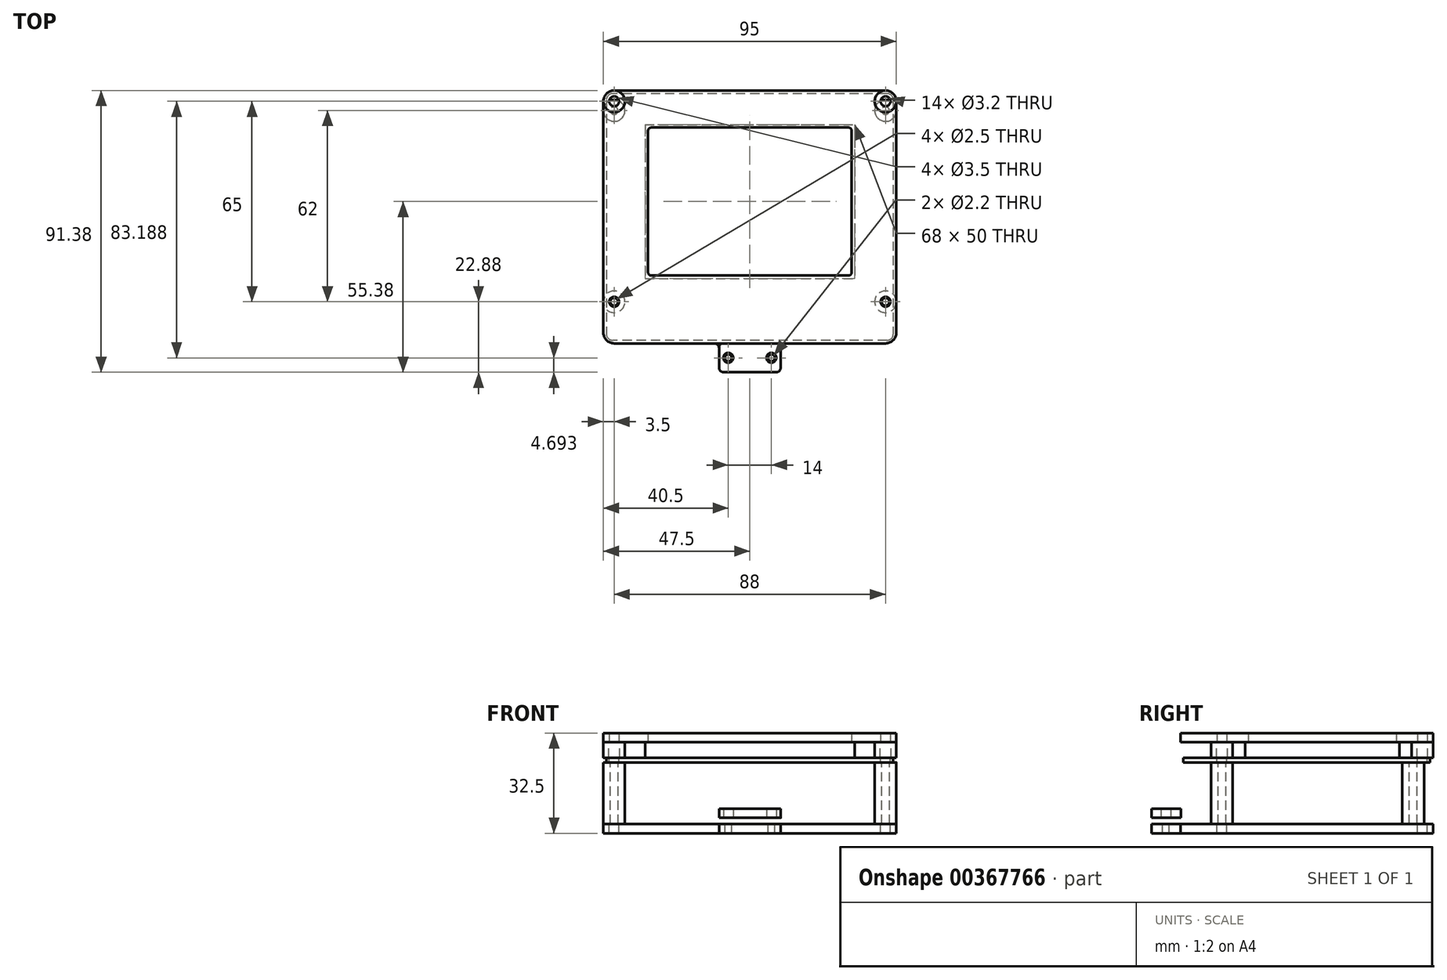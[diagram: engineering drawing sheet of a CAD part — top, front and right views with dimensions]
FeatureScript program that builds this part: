
annotation { "Feature Type Name" : "Feature", "Feature Type Description" : "" }
export const myFeature = defineFeature(function(context is Context, id is Id, definition is map)
    precondition{}
    {
        {
            var Q0;
            Q0=qCreatedBy(makeId("Top.planeOp"),FACE);
            var sketch = newSketch(context, id + "F0", { "sketchPlane" : qUnion([Q0])});
            skLineSegment(sketch, "E0.bottom", {"start": v(44, -41) * mm, "end": v(-44, -41) * mm});
            skLineSegment(sketch, "E0.top", {"start": v(44, 41) * mm, "end": v(-44, 41) * mm});
            skLineSegment(sketch, "E0.left", {"start": v(47.5, -37.5) * mm, "end": v(47.5, 37.5) * mm});
            skLineSegment(sketch, "E0.right", {"start": v(-47.5, -37.5) * mm, "end": v(-47.5, 37.5) * mm});
            skPoint(sketch, "E0.middle", {"position": v(0, 0) * mm});
            skLineSegment(sketch, "E1.top", {"start": v(44, 37.5) * mm, "end": v(-44, 37.5) * mm, "construction": true});
            skLineSegment(sketch, "E1.left", {"start": v(44, -27.5) * mm, "end": v(44, 37.5) * mm, "construction": true});
            skLineSegment(sketch, "E1.right", {"start": v(-44, -27.5) * mm, "end": v(-44, 37.5) * mm, "construction": true});
            skLineSegment(sketch, "E2", {"start": v(-44, -27.5) * mm, "end": v(44, -27.5) * mm, "construction": true});
            skPoint(sketch, "E1.bottom.end.orphan", {"position": v(-44, -37.5) * mm});
            skPoint(sketch, "E3.orphan", {"position": v(44, -37.5) * mm});
            skCircle(sketch, "E4", {"center": v(-44, 37.5) * mm, "radius": 1.6 * mm});
            skCircle(sketch, "E5", {"center": v(44, 37.5) * mm, "radius": 1.6 * mm});
            skCircle(sketch, "E6", {"center": v(44, -27.5) * mm, "radius": 1.6 * mm});
            skCircle(sketch, "E7", {"center": v(-44, -27.5) * mm, "radius": 1.6 * mm});
            skArc(sketch, "E8", {"start": v(-44, 41) * mm, "mid": v(-46.47, 39.97) * mm, "end": v(-47.5, 37.5) * mm});
            skArc(sketch, "E9", {"start": v(47.5, 37.5) * mm, "mid": v(46.47, 39.97) * mm, "end": v(44, 41) * mm});
            skPoint(sketch, "E10.visualSharp", {"position": v(47.5, -41) * mm});
            skArc(sketch, "E10.filletArc", {"start": v(44, -41) * mm, "mid": v(46.47, -39.97) * mm, "end": v(47.5, -37.5) * mm});
            skPoint(sketch, "E11.visualSharp", {"position": v(-47.5, -41) * mm});
            skArc(sketch, "E11.filletArc", {"start": v(-47.5, -37.5) * mm, "mid": v(-46.47, -39.97) * mm, "end": v(-44, -41) * mm});
            skPoint(sketch, "E12.orphan", {"position": v(-47.5, 41) * mm});
            skPoint(sketch, "E13.orphan", {"position": v(47.5, 41) * mm});
            skLineSegment(sketch, "E14.bottom", {"start": v(-32, 29) * mm, "end": v(32, 29) * mm});
            skLineSegment(sketch, "E14.top", {"start": v(-32, -19) * mm, "end": v(32, -19) * mm});
            skLineSegment(sketch, "E14.left", {"start": v(-33, 28) * mm, "end": v(-33, -18) * mm});
            skLineSegment(sketch, "E14.right", {"start": v(33, 28) * mm, "end": v(33, -18) * mm});
            skPoint(sketch, "E15.visualSharp", {"position": v(-33, 29) * mm});
            skArc(sketch, "E15.filletArc", {"start": v(-32, 29) * mm, "mid": v(-32.7, 28.7) * mm, "end": v(-33, 28) * mm});
            skPoint(sketch, "E16.visualSharp", {"position": v(33, 29) * mm});
            skArc(sketch, "E16.filletArc", {"start": v(33, 28) * mm, "mid": v(32.7, 28.7) * mm, "end": v(32, 29) * mm});
            skPoint(sketch, "E17.visualSharp", {"position": v(33, -19) * mm});
            skArc(sketch, "E17.filletArc", {"start": v(32, -19) * mm, "mid": v(32.7, -18.7) * mm, "end": v(33, -18) * mm});
            skPoint(sketch, "E18.visualSharp", {"position": v(-33, -19) * mm});
            skArc(sketch, "E18.filletArc", {"start": v(-33, -18) * mm, "mid": v(-32.7, -18.7) * mm, "end": v(-32, -19) * mm});
            skSolve(sketch);
        }
        {
            var Q0;
            Q0=makeQuery(id+"F0.imprint","IMPRINT",FACE,{"disambiguationData":[TD([[makeQuery(id+"F0.imprint","IMPRINT",EDGE,{"derivedFrom":sQuery(id+"F0.wireOp",EDGE,"E0.bottom")}),-1.0]])]});
            extrude(context, id + "F1", {"entities" : qUnion([Q0]), "depth" : 3 * mm});
        }
        {
            var Q0;
            Q0=makeQuery(id+"F1.opExtrude","CAP_FACE",FACE,{"disambiguationData":[OSD([sQuery(id+"F0.wireOp",EDGE,"E0.bottom"),sQuery(id+"F0.wireOp",EDGE,"E0.top"),sQuery(id+"F0.wireOp",EDGE,"E0.left"),sQuery(id+"F0.wireOp",EDGE,"E0.right"),sQuery(id+"F0.wireOp",EDGE,"E4"),sQuery(id+"F0.wireOp",EDGE,"E5"),sQuery(id+"F0.wireOp",EDGE,"E6"),sQuery(id+"F0.wireOp",EDGE,"E7"),sQuery(id+"F0.wireOp",EDGE,"E8"),sQuery(id+"F0.wireOp",EDGE,"E9"),sQuery(id+"F0.wireOp",EDGE,"E10.filletArc"),sQuery(id+"F0.wireOp",EDGE,"E11.filletArc"),sQuery(id+"F0.wireOp",EDGE,"E14.bottom"),sQuery(id+"F0.wireOp",EDGE,"E14.top"),sQuery(id+"F0.wireOp",EDGE,"E14.left"),sQuery(id+"F0.wireOp",EDGE,"E14.right"),sQuery(id+"F0.wireOp",EDGE,"E15.filletArc"),sQuery(id+"F0.wireOp",EDGE,"E16.filletArc"),sQuery(id+"F0.wireOp",EDGE,"E17.filletArc"),sQuery(id+"F0.wireOp",EDGE,"E18.filletArc")])],"isStart":true});
            var sketch = newSketch(context, id + "F2", { "sketchPlane" : qUnion([Q0])});
            skCircle(sketch, "E19", {"center": v(-44, 27.5) * mm, "radius": 1.75 * mm});
            skCircle(sketch, "E20", {"center": v(44, 27.5) * mm, "radius": 1.75 * mm});
            skCircle(sketch, "E21", {"center": v(44, -37.5) * mm, "radius": 1.75 * mm});
            skCircle(sketch, "E22", {"center": v(-44, -37.5) * mm, "radius": 1.75 * mm});
            skCircle(sketch, "E23", {"center": v(-44, -37.5) * mm, "radius": 3.5 * mm});
            skCircle(sketch, "E24", {"center": v(44, -37.5) * mm, "radius": 3.5 * mm});
            skCircle(sketch, "E25", {"center": v(44, 27.5) * mm, "radius": 3.5 * mm});
            skCircle(sketch, "E26", {"center": v(-44, 27.5) * mm, "radius": 3.5 * mm});
            skSolve(sketch);
        }
        {
            var Q0;
            Q0=qSketchRegion(id+"F2",true);
            extrude(context, id + "F3", {"entities" : qUnion([Q0]), "depth" : 5 * mm});
        }
        {
            var Q0;
            Q0=makeQuery(id+"F3.opExtrude","CAP_FACE",FACE,{"disambiguationData":[OSD([sQuery(id+"F2.wireOp",EDGE,"E19"),sQuery(id+"F2.wireOp",EDGE,"E26")])],"isStart":false});
            var sketch = newSketch(context, id + "F4", { "sketchPlane" : qUnion([Q0])});
            skLineSegment(sketch, "E27.bottom", {"start": v(44.5, -40) * mm, "end": v(-44.5, -40) * mm});
            skLineSegment(sketch, "E27.top", {"start": v(44.5, 40) * mm, "end": v(-44.5, 40) * mm});
            skLineSegment(sketch, "E27.left", {"start": v(46.5, -38) * mm, "end": v(46.5, 38) * mm});
            skLineSegment(sketch, "E27.right", {"start": v(-46.5, -38) * mm, "end": v(-46.5, 38) * mm});
            skPoint(sketch, "E27.middle", {"position": v(0, 0) * mm});
            skPoint(sketch, "E28.visualSharp", {"position": v(-46.5, 40) * mm});
            skArc(sketch, "E28.filletArc", {"start": v(-44.5, 40) * mm, "mid": v(-45.91, 39.41) * mm, "end": v(-46.5, 38) * mm});
            skPoint(sketch, "E29.visualSharp", {"position": v(46.5, 40) * mm});
            skArc(sketch, "E29.filletArc", {"start": v(46.5, 38) * mm, "mid": v(45.91, 39.41) * mm, "end": v(44.5, 40) * mm});
            skPoint(sketch, "E30.visualSharp", {"position": v(46.5, -40) * mm});
            skArc(sketch, "E30.filletArc", {"start": v(44.5, -40) * mm, "mid": v(45.91, -39.41) * mm, "end": v(46.5, -38) * mm});
            skPoint(sketch, "E31.visualSharp", {"position": v(-46.5, -40) * mm});
            skArc(sketch, "E31.filletArc", {"start": v(-46.5, -38) * mm, "mid": v(-45.91, -39.41) * mm, "end": v(-44.5, -40) * mm});
            skCircle(sketch, "E32", {"center": v(-44, 27.5) * mm, "radius": 1.6 * mm});
            skCircle(sketch, "E33.0.1.0", {"center": v(-44, -37.5) * mm, "radius": 1.6 * mm});
            skCircle(sketch, "E33.1.0.0", {"center": v(44, 27.5) * mm, "radius": 1.6 * mm});
            skCircle(sketch, "E33.1.1.0", {"center": v(44, -37.5) * mm, "radius": 1.6 * mm});
            skCircle(sketch, "E33.2.0.0", {"center": v(132, 27.5) * mm, "radius": 1.6 * mm});
            skCircle(sketch, "E33.2.1.0", {"center": v(132, -37.5) * mm, "radius": 1.6 * mm});
            skLineSegment(sketch, "E33.direction1", {"start": v(-44, 27.5) * mm, "end": v(44, 27.5) * mm, "construction": true});
            skLineSegment(sketch, "E33.direction2", {"start": v(-44, 27.5) * mm, "end": v(-44, -37.5) * mm, "construction": true});
            skSolve(sketch);
        }
        {
            var Q0;
            Q0=qSketchRegion(id+"F4",true);
            extrude(context, id + "F5", {"entities" : qUnion([Q0]), "depth" : 1.5 * mm});
        }
        {
            var Q0;
            Q0=makeQuery(id+"F5.opExtrude","CAP_FACE",FACE,{"disambiguationData":[OSD([sQuery(id+"F4.wireOp",EDGE,"E27.bottom"),sQuery(id+"F4.wireOp",EDGE,"E27.top"),sQuery(id+"F4.wireOp",EDGE,"E27.left"),sQuery(id+"F4.wireOp",EDGE,"E27.right"),sQuery(id+"F4.wireOp",EDGE,"E28.filletArc"),sQuery(id+"F4.wireOp",EDGE,"E29.filletArc"),sQuery(id+"F4.wireOp",EDGE,"E30.filletArc"),sQuery(id+"F4.wireOp",EDGE,"E31.filletArc"),sQuery(id+"F4.wireOp",EDGE,"E32"),sQuery(id+"F4.wireOp",EDGE,"E33.0.1.0"),sQuery(id+"F4.wireOp",EDGE,"E33.1.0.0"),sQuery(id+"F4.wireOp",EDGE,"E33.1.1.0")])],"isStart":false});
            var sketch = newSketch(context, id + "F6", { "sketchPlane" : qUnion([Q0])});
            skCircle(sketch, "E34", {"center": v(-44, 27.5) * mm, "radius": 1.25 * mm});
            skCircle(sketch, "E35", {"center": v(-44, 27.5) * mm, "radius": 3.5 * mm});
            skCircle(sketch, "E36.0.1.0", {"center": v(-44, -34.5) * mm, "radius": 1.25 * mm});
            skCircle(sketch, "E36.0.1.1", {"center": v(-44, -34.5) * mm, "radius": 3.5 * mm});
            skCircle(sketch, "E36.1.0.0", {"center": v(44, 27.5) * mm, "radius": 1.25 * mm});
            skCircle(sketch, "E36.1.0.1", {"center": v(44, 27.5) * mm, "radius": 3.5 * mm});
            skCircle(sketch, "E36.1.1.0", {"center": v(44, -34.5) * mm, "radius": 1.25 * mm});
            skCircle(sketch, "E36.1.1.1", {"center": v(44, -34.5) * mm, "radius": 3.5 * mm});
            skLineSegment(sketch, "E36.direction1", {"start": v(-44, 27.5) * mm, "end": v(44, 27.5) * mm, "construction": true});
            skLineSegment(sketch, "E36.direction2", {"start": v(-44, 27.5) * mm, "end": v(-44, -34.5) * mm, "construction": true});
            skSolve(sketch);
        }
        {
            var Q0;
            Q0=qSketchRegion(id+"F6",true);
            extrude(context, id + "F7", {"entities" : qUnion([Q0]), "depth" : 20 * mm});
        }
        {
            var Q0;
            Q0=makeQuery(id+"F7.opExtrude","CAP_FACE",FACE,{"disambiguationData":[OSD([sQuery(id+"F6.wireOp",EDGE,"E34"),sQuery(id+"F6.wireOp",EDGE,"E35")])],"isStart":false});
            var sketch = newSketch(context, id + "F8", { "sketchPlane" : qUnion([Q0])});
            skLineSegment(sketch, "E37.bottom", {"start": v(44, -41) * mm, "end": v(-44, -41) * mm});
            skLineSegment(sketch, "E37.top", {"start": v(44, 41) * mm, "end": v(11.5, 41) * mm});
            skLineSegment(sketch, "E37.left", {"start": v(47.5, -37.5) * mm, "end": v(47.5, 37.5) * mm});
            skLineSegment(sketch, "E37.right", {"start": v(-47.5, -37.5) * mm, "end": v(-47.5, 37.5) * mm});
            skPoint(sketch, "E37.middle", {"position": v(0, 0) * mm});
            skPoint(sketch, "E38.visualSharp", {"position": v(47.5, 41) * mm});
            skArc(sketch, "E38.filletArc", {"start": v(47.5, 37.5) * mm, "mid": v(46.47, 39.97) * mm, "end": v(44, 41) * mm});
            skPoint(sketch, "E39.visualSharp", {"position": v(47.5, -41) * mm});
            skArc(sketch, "E39.filletArc", {"start": v(44, -41) * mm, "mid": v(46.47, -39.97) * mm, "end": v(47.5, -37.5) * mm});
            skPoint(sketch, "E40.visualSharp", {"position": v(-47.5, -41) * mm});
            skArc(sketch, "E40.filletArc", {"start": v(-47.5, -37.5) * mm, "mid": v(-46.47, -39.97) * mm, "end": v(-44, -41) * mm});
            skPoint(sketch, "E41.visualSharp", {"position": v(-47.5, 41) * mm});
            skArc(sketch, "E41.filletArc", {"start": v(-44, 41) * mm, "mid": v(-46.47, 39.97) * mm, "end": v(-47.5, 37.5) * mm});
            skCircle(sketch, "E42", {"center": v(-44, 27.5) * mm, "radius": 1.6 * mm});
            skCircle(sketch, "E43.0.1.0", {"center": v(-44, -37.5) * mm, "radius": 1.6 * mm});
            skCircle(sketch, "E43.1.0.0", {"center": v(44, 27.5) * mm, "radius": 1.6 * mm});
            skCircle(sketch, "E43.1.1.0", {"center": v(44, -37.5) * mm, "radius": 1.6 * mm});
            skLineSegment(sketch, "E43.direction1", {"start": v(-44, 27.5) * mm, "end": v(44, 27.5) * mm, "construction": true});
            skLineSegment(sketch, "E43.direction2", {"start": v(-44, 27.5) * mm, "end": v(-44, -37.5) * mm, "construction": true});
            skLineSegment(sketch, "E44.top", {"start": v(8.5, 50.37) * mm, "end": v(-8.5, 50.37) * mm});
            skLineSegment(sketch, "E44.left", {"start": v(10, 42.5) * mm, "end": v(10, 48.87) * mm});
            skLineSegment(sketch, "E44.right", {"start": v(-10, 42.5) * mm, "end": v(-10, 48.87) * mm});
            skPoint(sketch, "E44.middle", {"position": v(0, 41) * mm});
            skPoint(sketch, "E44.bottom.end.orphan", {"position": v(-10, 31.62) * mm});
            skPoint(sketch, "E45.orphan", {"position": v(10, 31.62) * mm});
            skLineSegment(sketch, "E46.trimOffspring", {"start": v(-11.5, 41) * mm, "end": v(-44, 41) * mm});
            skPoint(sketch, "E47.visualSharp", {"position": v(-10, 41) * mm});
            skArc(sketch, "E47.filletArc", {"start": v(-11.5, 41) * mm, "mid": v(-10.44, 41.44) * mm, "end": v(-10, 42.5) * mm});
            skPoint(sketch, "E48.visualSharp", {"position": v(10, 41) * mm});
            skArc(sketch, "E48.filletArc", {"start": v(10, 42.5) * mm, "mid": v(10.44, 41.44) * mm, "end": v(11.5, 41) * mm});
            skPoint(sketch, "E49.visualSharp", {"position": v(10, 50.37) * mm});
            skArc(sketch, "E49.filletArc", {"start": v(10, 48.87) * mm, "mid": v(9.56, 49.94) * mm, "end": v(8.5, 50.37) * mm});
            skPoint(sketch, "E50.visualSharp", {"position": v(-10, 50.37) * mm});
            skArc(sketch, "E50.filletArc", {"start": v(-8.5, 50.37) * mm, "mid": v(-9.56, 49.94) * mm, "end": v(-10, 48.87) * mm});
            skLineSegment(sketch, "E51", {"start": v(-10, 45.69) * mm, "end": v(10, 45.69) * mm, "construction": true});
            skCircle(sketch, "E52", {"center": v(-7, 45.69) * mm, "radius": 1.1 * mm});
            skCircle(sketch, "E53", {"center": v(7, 45.69) * mm, "radius": 1.1 * mm});
            skSolve(sketch);
        }
        {
            var Q0;
            Q0=qSketchRegion(id+"F8",true);
            extrude(context, id + "F9", {"entities" : qUnion([Q0]), "depth" : 3 * mm});
        }
        {
            var Q0;
            Q0=makeQuery(id+"F9.opExtrude","CAP_FACE",FACE,{"disambiguationData":[OSD([sQuery(id+"F8.wireOp",EDGE,"E37.bottom"),sQuery(id+"F8.wireOp",EDGE,"E37.top"),sQuery(id+"F8.wireOp",EDGE,"E37.left"),sQuery(id+"F8.wireOp",EDGE,"E37.right"),sQuery(id+"F8.wireOp",EDGE,"E38.filletArc"),sQuery(id+"F8.wireOp",EDGE,"E39.filletArc"),sQuery(id+"F8.wireOp",EDGE,"E40.filletArc"),sQuery(id+"F8.wireOp",EDGE,"E41.filletArc"),sQuery(id+"F8.wireOp",EDGE,"E42"),sQuery(id+"F8.wireOp",EDGE,"E43.0.1.0"),sQuery(id+"F8.wireOp",EDGE,"E43.1.0.0"),sQuery(id+"F8.wireOp",EDGE,"E43.1.1.0"),sQuery(id+"F8.wireOp",EDGE,"E44.top"),sQuery(id+"F8.wireOp",EDGE,"E44.left"),sQuery(id+"F8.wireOp",EDGE,"E44.right"),sQuery(id+"F8.wireOp",EDGE,"E46.trimOffspring"),sQuery(id+"F8.wireOp",EDGE,"E47.filletArc"),sQuery(id+"F8.wireOp",EDGE,"E48.filletArc"),sQuery(id+"F8.wireOp",EDGE,"E49.filletArc"),sQuery(id+"F8.wireOp",EDGE,"E50.filletArc"),sQuery(id+"F8.wireOp",EDGE,"E52"),sQuery(id+"F8.wireOp",EDGE,"E53")])],"isStart":true});
            cPlane(context, id + "F10", {"entities" : qUnion([Q0]), "cplaneType" : CPlaneType.OFFSET, "offset" : 2 * mm, "width" : 150 * mm, "height" : 150 * mm});
        }
        {
            var Q0;
            Q0=qCreatedBy(id+"F10.planeOp",FACE);
            var sketch = newSketch(context, id + "F11", { "sketchPlane" : qUnion([Q0])});
            skLineSegment(sketch, "E54.0", {"start": v(10, -42.37) * mm, "end": v(10, -48.87) * mm});
            skLineSegment(sketch, "E55.0", {"start": v(8.5, -50.37) * mm, "end": v(-8.5, -50.37) * mm});
            skLineSegment(sketch, "E56.0", {"start": v(-10, -42.37) * mm, "end": v(-10, -48.87) * mm});
            skLineSegment(sketch, "E57", {"start": v(-8.5, -40.87) * mm, "end": v(8.5, -40.87) * mm});
            skPoint(sketch, "E58.newPointA", {"position": v(10, -48.87) * mm});
            skPoint(sketch, "E58.newPointB", {"position": v(8.5, -50.37) * mm});
            skArc(sketch, "E58.filletArc", {"start": v(8.5, -50.37) * mm, "mid": v(9.56, -49.94) * mm, "end": v(10, -48.87) * mm});
            skPoint(sketch, "E59.newPointA", {"position": v(-8.5, -50.37) * mm});
            skPoint(sketch, "E59.newPointB", {"position": v(-10, -48.87) * mm});
            skArc(sketch, "E59.filletArc", {"start": v(-10, -48.87) * mm, "mid": v(-9.56, -49.94) * mm, "end": v(-8.5, -50.37) * mm});
            skPoint(sketch, "E60.newPointA", {"position": v(-10, -42.5) * mm});
            skArc(sketch, "E60.filletArc", {"start": v(-8.5, -40.87) * mm, "mid": v(-9.56, -41.31) * mm, "end": v(-10, -42.37) * mm});
            skPoint(sketch, "E61.newPointB", {"position": v(10, -42.5) * mm});
            skArc(sketch, "E61.filletArc", {"start": v(10, -42.37) * mm, "mid": v(9.56, -41.31) * mm, "end": v(8.5, -40.88) * mm});
            skCircle(sketch, "E62", {"center": v(-7, -45.69) * mm, "radius": 1.6 * mm});
            skCircle(sketch, "E63", {"center": v(7, -45.69) * mm, "radius": 1.6 * mm});
            skSolve(sketch);
        }
        {
            var Q0;
            Q0=qSketchRegion(id+"F11",true);
            extrude(context, id + "F12", {"entities" : qUnion([Q0]), "depth" : 3 * mm});
        }
        {
            var Q0;
            Q0=makeQuery(id+"F5.opExtrude","CAP_FACE",FACE,{"disambiguationData":[OSD([sQuery(id+"F4.wireOp",EDGE,"E27.bottom"),sQuery(id+"F4.wireOp",EDGE,"E27.top"),sQuery(id+"F4.wireOp",EDGE,"E27.left"),sQuery(id+"F4.wireOp",EDGE,"E27.right"),sQuery(id+"F4.wireOp",EDGE,"E28.filletArc"),sQuery(id+"F4.wireOp",EDGE,"E29.filletArc"),sQuery(id+"F4.wireOp",EDGE,"E30.filletArc"),sQuery(id+"F4.wireOp",EDGE,"E31.filletArc"),sQuery(id+"F4.wireOp",EDGE,"E32"),sQuery(id+"F4.wireOp",EDGE,"E33.0.1.0"),sQuery(id+"F4.wireOp",EDGE,"E33.1.0.0"),sQuery(id+"F4.wireOp",EDGE,"E33.1.1.0")])],"isStart":true});
            var sketch = newSketch(context, id + "F13", { "sketchPlane" : qUnion([Q0])});
            skLineSegment(sketch, "E64.bottom", {"start": v(-34, 30) * mm, "end": v(34, 30) * mm});
            skLineSegment(sketch, "E64.top", {"start": v(-34, -20) * mm, "end": v(34, -20) * mm});
            skLineSegment(sketch, "E64.left", {"start": v(-34, 30) * mm, "end": v(-34, -20) * mm});
            skLineSegment(sketch, "E64.right", {"start": v(34, 30) * mm, "end": v(34, -20) * mm});
            skSolve(sketch);
        }
        {
            var Q0;
            Q0=qSketchRegion(id+"F13",true);
            var Q1;
            Q1=makeQuery(id+"F1.opExtrude","CAP_FACE",FACE,{"disambiguationData":[OSD([sQuery(id+"F0.wireOp",EDGE,"E0.bottom"),sQuery(id+"F0.wireOp",EDGE,"E0.top"),sQuery(id+"F0.wireOp",EDGE,"E0.left"),sQuery(id+"F0.wireOp",EDGE,"E0.right"),sQuery(id+"F0.wireOp",EDGE,"E4"),sQuery(id+"F0.wireOp",EDGE,"E5"),sQuery(id+"F0.wireOp",EDGE,"E6"),sQuery(id+"F0.wireOp",EDGE,"E7"),sQuery(id+"F0.wireOp",EDGE,"E8"),sQuery(id+"F0.wireOp",EDGE,"E9"),sQuery(id+"F0.wireOp",EDGE,"E10.filletArc"),sQuery(id+"F0.wireOp",EDGE,"E11.filletArc"),sQuery(id+"F0.wireOp",EDGE,"E14.bottom"),sQuery(id+"F0.wireOp",EDGE,"E14.top"),sQuery(id+"F0.wireOp",EDGE,"E14.left"),sQuery(id+"F0.wireOp",EDGE,"E14.right"),sQuery(id+"F0.wireOp",EDGE,"E15.filletArc"),sQuery(id+"F0.wireOp",EDGE,"E16.filletArc"),sQuery(id+"F0.wireOp",EDGE,"E17.filletArc"),sQuery(id+"F0.wireOp",EDGE,"E18.filletArc")])],"isStart":true});
            extrude(context, id + "F14", {"entities" : qUnion([Q0]), "operationType" : NewBodyOperationType.ADD, "endBound" : BoundingType.UP_TO_SURFACE, "endBoundEntityFace" : qUnion([Q1]), "depth" : 25 * mm});
        }
        {
            var Q0;
            Q0=makeQuery(id+"F5.opExtrude","SWEPT_BODY",BODY,{"disambiguationData":[OSD([sQuery(id+"F4.wireOp",EDGE,"E33.2.0.0")])]});
            deleteBodies(context, id + "F15", {"entities" : qUnion([Q0])});
        }
        {
            var Q0;
            Q0=makeQuery(id+"F5.opExtrude","SWEPT_BODY",BODY,{"disambiguationData":[OSD([sQuery(id+"F4.wireOp",EDGE,"E33.2.1.0")])]});
            deleteBodies(context, id + "F16", {"entities" : qUnion([Q0])});
        }
    });
